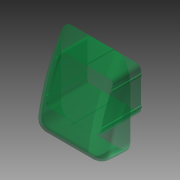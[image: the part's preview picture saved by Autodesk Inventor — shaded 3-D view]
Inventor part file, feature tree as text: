
AUTODESK INVENTOR PART (.ipt)
format: ipt  version: 2015 (Build 190159000, 159)  size: 606,208 bytes
history: native  units: in
note: dims shown in document units (in); Inventor stores cm internally (conversion verified against a paired STEP export)
features: sketch x2, extrude x2, fillet x2, plane x1, shell x1
ambient origin geometry x8: Origin, YZ Plane, XZ Plane, XY Plane, X Axis, Y Axis, Z Axis, Center Point
bodies: Solid1 (feature_tree)
feature tree (8):
  sketch  "Sketch1"  dims[d0=1.97in d1=1.54in d2=0.15in d3=0.67in]
  plane  "Work Plane1"
  extrude  "Extrusion1"  Depth=1.54in
  fillet  "Fillet1"  Radius=0.15in
  shell  "Shell1"  Thickness=0.67in
  extrude  "Extrusion2"  Depth=1.0in
  fillet  "Fillet2"  Radius=0.4in
  sketch  "Sketch2"  dims[d5=3.04in d6=1.0in d7=0.4in d8=6.0in d9=6.0in d10=0.825in d11=2.55in d12=0.0in d13=0.5in d14=0.07in d15=2.55in d16=0.0in d19=0.044in d20=0.05in d21=0.25in d22=0.25in d23=0.05in d24=0.05in d25=0.01in]
